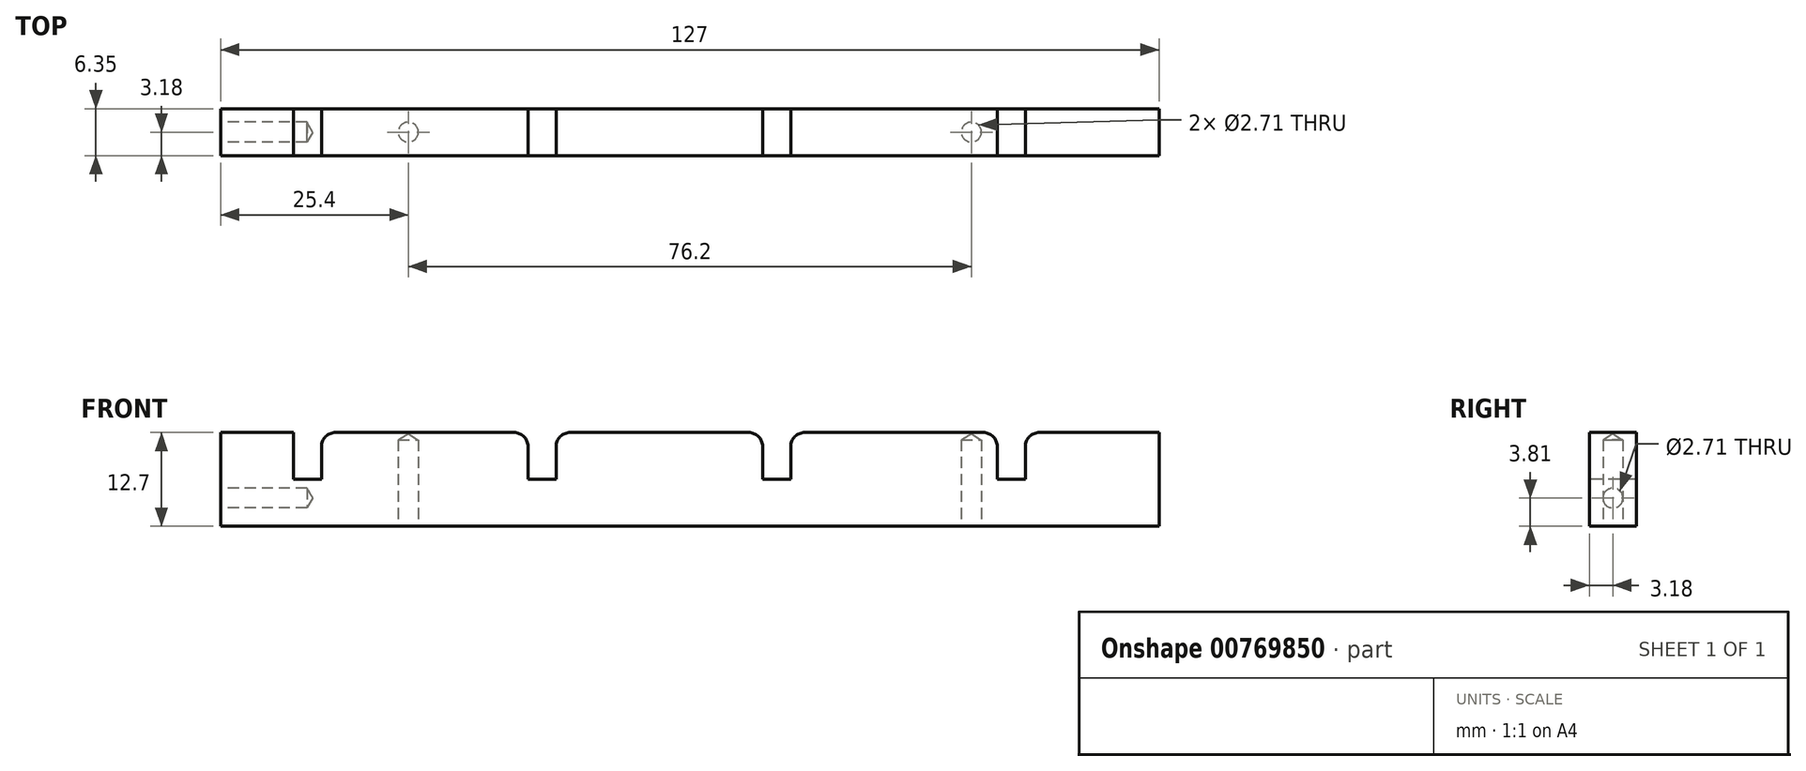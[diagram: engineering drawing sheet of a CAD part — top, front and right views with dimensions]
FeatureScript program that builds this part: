
annotation { "Feature Type Name" : "Feature", "Feature Type Description" : "" }
export const myFeature = defineFeature(function(context is Context, id is Id, definition is map)
    precondition{}
    {
        {
            var Q0;
            Q0=qCreatedBy(makeId("Top.planeOp"),FACE);
            var sketch = newSketch(context, id + "F0", { "sketchPlane" : qUnion([Q0])});
            skLineSegment(sketch, "E0.bottom", {"start": v(-63.5, 3.18) * mm, "end": v(63.5, 3.18) * mm});
            skLineSegment(sketch, "E0.top", {"start": v(-63.5, -3.17) * mm, "end": v(63.5, -3.17) * mm});
            skLineSegment(sketch, "E0.left", {"start": v(-63.5, 3.18) * mm, "end": v(-63.5, -3.17) * mm});
            skLineSegment(sketch, "E0.right", {"start": v(63.5, 3.18) * mm, "end": v(63.5, -3.17) * mm});
            skLineSegment(sketch, "E1", {"start": v(-63.5, 3.18) * mm, "end": v(63.5, -3.17) * mm, "construction": true});
            skPoint(sketch, "E2", {"position": v(0, 0) * mm});
            skSolve(sketch);
        }
        {
            var Q0;
            Q0 = qSketchRegion(id + "F0", true);
            extrude(context, id + "F1", {"entities" : qUnion([Q0]), "depth" : 12.7 * mm, "offsetDistance" : 25.4 * mm});
        }
        {
            var Q0;
            Q0=makeQuery(id+"F1.opExtrude","SWEPT_FACE",FACE,{"disambiguationData":[OSD([sQuery(id+"F0.wireOp",EDGE,"E0.top")])]});
            var sketch = newSketch(context, id + "F2", { "sketchPlane" : qUnion([Q0])});
            skLineSegment(sketch, "E3", {"start": v(-63.5, 6.35) * mm, "end": v(63.5, 6.35) * mm, "construction": true});
            skLineSegment(sketch, "E4", {"start": v(-53.66, 12.7) * mm, "end": v(-53.66, 6.35) * mm});
            skLineSegment(sketch, "E5", {"start": v(-53.66, 6.35) * mm, "end": v(-49.85, 6.35) * mm});
            skLineSegment(sketch, "E6", {"start": v(-49.85, 6.35) * mm, "end": v(-49.85, 12.7) * mm});
            skLineSegment(sketch, "E7", {"start": v(-53.66, 12.7) * mm, "end": v(-49.85, 12.7) * mm});
            skLineSegment(sketch, "E8.1.0.0", {"start": v(-21.9, 12.7) * mm, "end": v(-18.1, 12.7) * mm});
            skLineSegment(sketch, "E8.1.0.1", {"start": v(-21.9, 12.7) * mm, "end": v(-21.9, 6.35) * mm});
            skLineSegment(sketch, "E8.1.0.2", {"start": v(-18.1, 6.35) * mm, "end": v(-18.1, 12.7) * mm});
            skLineSegment(sketch, "E8.1.0.3", {"start": v(-21.9, 6.35) * mm, "end": v(-18.1, 6.35) * mm});
            skLineSegment(sketch, "E8.2.0.0", {"start": v(9.84, 12.7) * mm, "end": v(13.65, 12.7) * mm});
            skLineSegment(sketch, "E8.2.0.1", {"start": v(9.84, 12.7) * mm, "end": v(9.84, 6.35) * mm});
            skLineSegment(sketch, "E8.2.0.2", {"start": v(13.65, 6.35) * mm, "end": v(13.65, 12.7) * mm});
            skLineSegment(sketch, "E8.2.0.3", {"start": v(9.84, 6.35) * mm, "end": v(13.65, 6.35) * mm});
            skLineSegment(sketch, "E8.3.0.0", {"start": v(41.6, 12.7) * mm, "end": v(45.4, 12.7) * mm});
            skLineSegment(sketch, "E8.3.0.1", {"start": v(41.6, 12.7) * mm, "end": v(41.6, 6.35) * mm});
            skLineSegment(sketch, "E8.3.0.2", {"start": v(45.4, 6.35) * mm, "end": v(45.4, 12.7) * mm});
            skLineSegment(sketch, "E8.3.0.3", {"start": v(41.6, 6.35) * mm, "end": v(45.4, 6.35) * mm});
            skLineSegment(sketch, "E8.direction1", {"start": v(-53.66, 6.35) * mm, "end": v(-21.9, 6.35) * mm, "construction": true});
            skPoint(sketch, "E9", {"position": v(-51.75, 6.35) * mm});
            skSolve(sketch);
        }
        {
            var Q0;
            Q0 = qSketchRegion(id + "F2", true);
            extrude(context, id + "F3", {"entities" : qUnion([Q0]), "operationType" : NewBodyOperationType.REMOVE, "endBound" : BoundingType.UP_TO_NEXT, "oppositeDirection" : true, "depth" : 25.4 * mm, "offsetDistance" : 25.4 * mm});
        }
        {
            var Q0;
            Q0=makeQuery(id+"F3.boolean.opBoolean","COPY",EDGE,{"derivedFrom":makeQuery(id+"F3.opExtrude","SWEPT_EDGE",EDGE,{"disambiguationData":[OSD([sQuery(id+"F0.wireOp",EDGE,"E0.top"),sQuery(id+"F2.wireOp",EDGE,"E4"),sQuery(id+"F2.wireOp",EDGE,"E7")])]})});
            var Q1;
            Q1=makeQuery(id+"F3.boolean.opBoolean","COPY",EDGE,{"derivedFrom":makeQuery(id+"F3.opExtrude","SWEPT_EDGE",EDGE,{"disambiguationData":[OSD([sQuery(id+"F0.wireOp",EDGE,"E0.top"),sQuery(id+"F2.wireOp",EDGE,"E6"),sQuery(id+"F2.wireOp",EDGE,"E7")])]})});
            var Q2;
            Q2=makeQuery(id+"F3.boolean.opBoolean","COPY",EDGE,{"derivedFrom":makeQuery(id+"F3.opExtrude","SWEPT_EDGE",EDGE,{"disambiguationData":[OSD([sQuery(id+"F0.wireOp",EDGE,"E0.top"),sQuery(id+"F2.wireOp",EDGE,"E8.1.0.0"),sQuery(id+"F2.wireOp",EDGE,"E8.1.0.1")])]})});
            var Q3;
            Q3=makeQuery(id+"F3.boolean.opBoolean","COPY",EDGE,{"derivedFrom":makeQuery(id+"F3.opExtrude","SWEPT_EDGE",EDGE,{"disambiguationData":[OSD([sQuery(id+"F0.wireOp",EDGE,"E0.top"),sQuery(id+"F2.wireOp",EDGE,"E8.1.0.0"),sQuery(id+"F2.wireOp",EDGE,"E8.1.0.2")])]})});
            var Q4;
            Q4=makeQuery(id+"F3.boolean.opBoolean","COPY",EDGE,{"derivedFrom":makeQuery(id+"F3.opExtrude","SWEPT_EDGE",EDGE,{"disambiguationData":[OSD([sQuery(id+"F0.wireOp",EDGE,"E0.top"),sQuery(id+"F2.wireOp",EDGE,"E8.2.0.0"),sQuery(id+"F2.wireOp",EDGE,"E8.2.0.1")])]})});
            var Q5;
            Q5=makeQuery(id+"F3.boolean.opBoolean","COPY",EDGE,{"derivedFrom":makeQuery(id+"F3.opExtrude","SWEPT_EDGE",EDGE,{"disambiguationData":[OSD([sQuery(id+"F0.wireOp",EDGE,"E0.top"),sQuery(id+"F2.wireOp",EDGE,"E8.2.0.0"),sQuery(id+"F2.wireOp",EDGE,"E8.2.0.2")])]})});
            var Q6;
            Q6=makeQuery(id+"F3.boolean.opBoolean","COPY",EDGE,{"derivedFrom":makeQuery(id+"F3.opExtrude","SWEPT_EDGE",EDGE,{"disambiguationData":[OSD([sQuery(id+"F0.wireOp",EDGE,"E0.top"),sQuery(id+"F2.wireOp",EDGE,"E8.3.0.0"),sQuery(id+"F2.wireOp",EDGE,"E8.3.0.1")])]})});
            var Q7;
            Q7=makeQuery(id+"F3.boolean.opBoolean","COPY",EDGE,{"derivedFrom":makeQuery(id+"F3.opExtrude","SWEPT_EDGE",EDGE,{"disambiguationData":[OSD([sQuery(id+"F0.wireOp",EDGE,"E0.top"),sQuery(id+"F2.wireOp",EDGE,"E8.3.0.0"),sQuery(id+"F2.wireOp",EDGE,"E8.3.0.2")])]})});
            fillet(context, id + "F4", {"entities" : qUnion([Q0, Q1, Q2, Q3, Q4, Q5, Q6, Q7]), "radius" : 1.9 * mm, "tangentPropagation" : true, "allowEdgeOverflow" : false});
        }
        {
            var Q0;
            Q0=makeQuery(id+"F1.opExtrude","CAP_FACE",FACE,{"disambiguationData":[OSD([sQuery(id+"F0.wireOp",EDGE,"E0.bottom"),sQuery(id+"F0.wireOp",EDGE,"E0.top"),sQuery(id+"F0.wireOp",EDGE,"E0.left"),sQuery(id+"F0.wireOp",EDGE,"E0.right")])],"isStart":true});
            var sketch = newSketch(context, id + "F5", { "sketchPlane" : qUnion([Q0])});
            skLineSegment(sketch, "E10", {"start": v(-63.5, 0) * mm, "end": v(63.5, 0) * mm, "construction": true});
            skPoint(sketch, "E11", {"position": v(-38.1, 0) * mm});
            skPoint(sketch, "E12", {"position": v(38.1, 0) * mm});
            skSolve(sketch);
        }
        {
            var Q0;
            Q0=makeQuery(id+"F1.opExtrude","SWEPT_FACE",FACE,{"disambiguationData":[OSD([sQuery(id+"F0.wireOp",EDGE,"E0.left")])]});
            var sketch = newSketch(context, id + "F6", { "sketchPlane" : qUnion([Q0])});
            skLineSegment(sketch, "E13", {"start": v(0, 12.7) * mm, "end": v(0, 0) * mm, "construction": true});
            skPoint(sketch, "E14", {"position": v(0, 3.81) * mm});
            skSolve(sketch);
        }
        {
            var Q0;
            Q0=sQuery(id+"F5.wireOp",VERTEX,"E11");
            var Q1;
            Q1=sQuery(id+"F5.wireOp",VERTEX,"E12");
            var Q2;
            Q2=sQuery(id+"F6.wireOp",VERTEX,"E14");
            var Q3;
            Q3=makeQuery(id+"F1.opExtrude","SWEPT_BODY",BODY,{"disambiguationData":[OSD([sQuery(id+"F0.wireOp",EDGE,"E0.bottom"),sQuery(id+"F0.wireOp",EDGE,"E0.top"),sQuery(id+"F0.wireOp",EDGE,"E0.left"),sQuery(id+"F0.wireOp",EDGE,"E0.right")])]});
            hole(context, id + "F7", {"style" : HoleStyle.SIMPLE, "endStyle" : HoleEndStyle.BLIND, "standardTappedOrClearance" : lookupTablePath({ "standard" : "ANSI", "engagement" : "75%", "pitch" : "32 tpi", "size" : "#6", "type" : "Tapped" }), "standardBlindInLast" : lookupTablePath({ "standard" : "ANSI", "engagement" : "75%", "pitch" : "32 tpi", "size" : "#6", "type" : "Tapped" }), "holeDiameter" : 2.7 * mm, "majorDiameter" : 3.5 * mm, "showTappedDepth" : true, "holeDepth" : 11.68 * mm, "tappedDepth" : 9.3 * mm, "tapClearance" : 3, "locations" : qUnion([Q0, Q1, Q2]), "scope" : qUnion([Q3])});
        }
    });
